# Revit family: 01302_PDI
name_source: partatom
category: Air Terminals
revit_build: Autodesk Revit MEP 2012 (Build: 20110309_2315(x64)
units: mm (PartAtom-declared; Revit-internal decimal feet)

## types (4) — shared parameters
Description = Difusor perforado
Funcion = Inyeccion
Manufacturer = INNES
Material = Alum/Acero/Inox
Model = PDI
Nota_Cuello = .
Nota_Modulo = .
Nota_SCuello = Cuello Redondo
Posicion de Instalacion = Techo
Redondo(1)Cuadrado(2) = 1
Seleccion_Cuello = 1
Tipo de Cuello = Redondo/Cuadrado/Rectangular
Type Comments = Deflector de aleta curva montado en el cuello
URL = https://www.innes.com.mx
Visible_Conector_C = No
Visible_Conector_R = Yes
Visible_MTexto = No
Visible_STexto = No
Visible_Texto_Cuello = No

## per-type parameters (varying)
| type | Conect_Cuadrado | Conect_Redondo | Cuello Min-Max Cuadrado | Cuello Min-Max Redondo | Cuello Min-Max Retangular | Medida_Requerida | Modulo | Modulo_Real | Var1 | Var2 | Var3 |
| PDI-12x12 | 7 7/8" | 3 15/16" | 6"x6" a 18"x18" en Incrementos de 2" | 6" hasta 18" en Incrementos de 2" | 8"x6" hasta 18"x16" en Incrementos de 2" | 8" | 12 | 12 | 8 | 8" | 8" |
| PDI-16x16 | 11 7/8" | 5 15/16" | 6"x6" a 18"x18" en Incrementos de 2" | 6" hasta 18" en Incrementos de 2" | 8"x6" hasta 18"x16" en Incrementos de 2" | 12" | 16 | 16 | 12 | 12" | 12" |
| PDI-20x20 | 13 7/8" | 6 15/16" | 6x6 a 18x18" en Incrementos de 2" | 6 hasta 18" en Incrementos de 2" |  | 14" | 20 | 20 | 14 | 14" | 14" |
| PDI-24x24 | 15 7/8" | 7 15/16" | 6"x6" a 18"x18" en Incrementos de 2" | 6" hasta 18" en Incrementos de 2" | 8"x6" hasta 18"x16" en Incrementos de 2" | 16" | 24 | 24 | 16 | 16" | 16" |

## geometry (parser evidence)
native form markers: Blend x5, Sweep x10
no freeform markers — native parametric forms only
